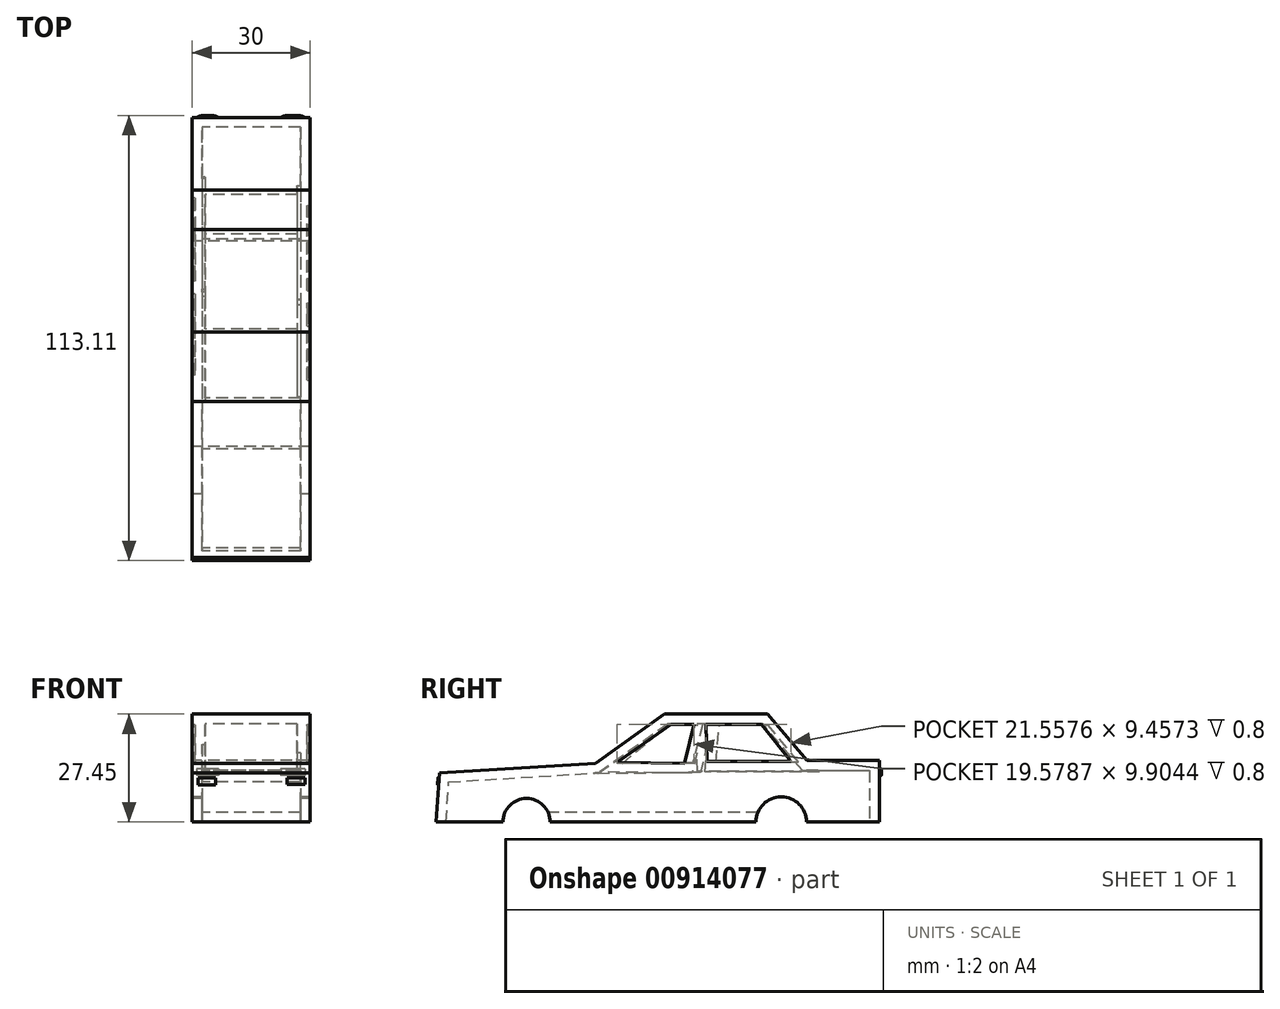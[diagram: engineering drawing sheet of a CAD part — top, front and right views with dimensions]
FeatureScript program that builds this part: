
annotation { "Feature Type Name" : "Feature", "Feature Type Description" : "" }
export const myFeature = defineFeature(function(context is Context, id is Id, definition is map)
    precondition{}
    {
        {
            var Q0;
            Q0=qCreatedBy(makeId("Right.planeOp"),FACE);
            var sketch = newSketch(context, id + "F0", { "sketchPlane" : qUnion([Q0])});
            skLineSegment(sketch, "E0", {"start": v(-54.31, 0) * mm, "end": v(-14.72, 2.41) * mm});
            skLineSegment(sketch, "E1", {"start": v(-14.72, 2.41) * mm, "end": v(2.91, 14.89) * mm});
            skLineSegment(sketch, "E2", {"start": v(2.91, 14.89) * mm, "end": v(29.03, 14.89) * mm});
            skLineSegment(sketch, "E3", {"start": v(29.03, 14.89) * mm, "end": v(39, 3.08) * mm});
            skLineSegment(sketch, "E4", {"start": v(39, 3.08) * mm, "end": v(57.47, 3.08) * mm});
            skLineSegment(sketch, "E5", {"start": v(57.47, 3.08) * mm, "end": v(57.47, -12.56) * mm});
            skLineSegment(sketch, "E6", {"start": v(57.47, -12.56) * mm, "end": v(-55.14, -12.56) * mm});
            skLineSegment(sketch, "E7", {"start": v(-55.14, -12.56) * mm, "end": v(-54.31, 0) * mm});
            skCircle(sketch, "E8", {"center": v(-32.19, -12.56) * mm, "radius": 6 * mm});
            skCircle(sketch, "E9", {"center": v(32.52, -12.56) * mm, "radius": 6.42 * mm});
            skSolve(sketch);
        }
        {
            var Q0;
            Q0=makeQuery(id+"F0.imprint","IMPRINT",FACE,{"disambiguationData":[TD([[makeQuery(id+"F0.imprint","IMPRINT",EDGE,{"derivedFrom":sQuery(id+"F0.wireOp",EDGE,"E0")}),-1.0]])]});
            extrude(context, id + "F1", {"entities" : qUnion([Q0]), "endBound" : BoundingType.SYMMETRIC, "depth" : 30 * mm, "offsetDistance" : 25 * mm});
        }
        {
            var Q0;
            Q0=makeQuery(id+"F1.opExtrude","CAP_FACE",FACE,{"disambiguationData":[OSD([sQuery(id+"F0.wireOp",EDGE,"E0"),sQuery(id+"F0.wireOp",EDGE,"E1"),sQuery(id+"F0.wireOp",EDGE,"E2"),sQuery(id+"F0.wireOp",EDGE,"E3"),sQuery(id+"F0.wireOp",EDGE,"E4"),sQuery(id+"F0.wireOp",EDGE,"E5"),sQuery(id+"F0.wireOp",EDGE,"E6"),sQuery(id+"F0.wireOp",EDGE,"E7"),sQuery(id+"F0.wireOp",EDGE,"E8"),sQuery(id+"F0.wireOp",EDGE,"E9")])],"isStart":false});
            var sketch = newSketch(context, id + "F2", { "sketchPlane" : qUnion([Q0])});
            skLineSegment(sketch, "E10", {"start": v(-9.25, 2.63) * mm, "end": v(4.45, 12.32) * mm});
            skLineSegment(sketch, "E11", {"start": v(4.45, 12.32) * mm, "end": v(10.33, 12.32) * mm});
            skLineSegment(sketch, "E12", {"start": v(10.33, 12.32) * mm, "end": v(7.91, 2.41) * mm});
            skLineSegment(sketch, "E13", {"start": v(7.91, 2.41) * mm, "end": v(-9.25, 2.63) * mm});
            skLineSegment(sketch, "E14", {"start": v(13.45, 12.32) * mm, "end": v(27.52, 12.32) * mm});
            skLineSegment(sketch, "E15", {"start": v(27.52, 12.32) * mm, "end": v(35, 2.86) * mm});
            skLineSegment(sketch, "E16", {"start": v(35, 2.86) * mm, "end": v(13.68, 2.86) * mm});
            skLineSegment(sketch, "E17", {"start": v(13.68, 2.86) * mm, "end": v(13.45, 12.32) * mm});
            skLineSegment(sketch, "E18.bottom", {"start": v(23.6, 12.32) * mm, "end": v(25.34, 12.32) * mm});
            skLineSegment(sketch, "E18.top", {"start": v(23.6, 2.86) * mm, "end": v(25.34, 2.86) * mm});
            skLineSegment(sketch, "E18.left", {"start": v(23.6, 12.32) * mm, "end": v(23.6, 2.86) * mm});
            skLineSegment(sketch, "E18.right", {"start": v(25.34, 12.32) * mm, "end": v(25.34, 2.86) * mm});
            skSolve(sketch);
        }
        {
            var Q0;
            Q0=makeQuery(id+"F2.imprint","IMPRINT",FACE,{"disambiguationData":[TD([[makeQuery(id+"F2.imprint","IMPRINT",EDGE,{"derivedFrom":sQuery(id+"F2.wireOp",EDGE,"E10")}),-1.0]])]});
            var Q1;
            Q1=makeQuery(id+"F2.imprint","IMPRINT",FACE,{"disambiguationData":[TD([[makeQuery(id+"F2.imprint","IMPRINT",EDGE,{"derivedFrom":sQuery(id+"F2.wireOp",EDGE,"E14")}),-1.0]])]});
            extrude(context, id + "F3", {"entities" : qUnion([Q0, Q1]), "operationType" : NewBodyOperationType.REMOVE, "oppositeDirection" : true, "depth" : 0.8 * mm, "offsetDistance" : 25 * mm});
        }
        {
            var Q0;
            Q0=makeQuery(id+"F1.opExtrude","CAP_FACE",FACE,{"disambiguationData":[OSD([sQuery(id+"F0.wireOp",EDGE,"E0"),sQuery(id+"F0.wireOp",EDGE,"E1"),sQuery(id+"F0.wireOp",EDGE,"E2"),sQuery(id+"F0.wireOp",EDGE,"E3"),sQuery(id+"F0.wireOp",EDGE,"E4"),sQuery(id+"F0.wireOp",EDGE,"E5"),sQuery(id+"F0.wireOp",EDGE,"E6"),sQuery(id+"F0.wireOp",EDGE,"E7"),sQuery(id+"F0.wireOp",EDGE,"E8"),sQuery(id+"F0.wireOp",EDGE,"E9")])],"isStart":true});
            var sketch = newSketch(context, id + "F4", { "sketchPlane" : qUnion([Q0])});
            skLineSegment(sketch, "E19", {"start": v(7.98, 2.3) * mm, "end": v(-3.78, 12.1) * mm});
            skLineSegment(sketch, "E20", {"start": v(-3.78, 12.1) * mm, "end": v(-12.55, 12.1) * mm});
            skLineSegment(sketch, "E21", {"start": v(-12.55, 12.1) * mm, "end": v(-10.01, 2.52) * mm});
            skLineSegment(sketch, "E22", {"start": v(-10.01, 2.52) * mm, "end": v(7.98, 2.3) * mm});
            skLineSegment(sketch, "E23", {"start": v(-16.81, 12.1) * mm, "end": v(-29.03, 12.1) * mm});
            skLineSegment(sketch, "E24", {"start": v(-29.03, 12.1) * mm, "end": v(-36.9, 2.64) * mm});
            skLineSegment(sketch, "E25", {"start": v(-36.9, 2.64) * mm, "end": v(-15.9, 2.64) * mm});
            skLineSegment(sketch, "E26", {"start": v(-15.9, 2.64) * mm, "end": v(-16.81, 12.1) * mm});
            skLineSegment(sketch, "E27.bottom", {"start": v(-26.48, 12.1) * mm, "end": v(-24.63, 12.1) * mm});
            skLineSegment(sketch, "E27.top", {"start": v(-26.48, 2.64) * mm, "end": v(-24.63, 2.64) * mm});
            skLineSegment(sketch, "E27.left", {"start": v(-26.48, 12.1) * mm, "end": v(-26.48, 2.64) * mm});
            skLineSegment(sketch, "E27.right", {"start": v(-24.63, 12.1) * mm, "end": v(-24.63, 2.64) * mm});
            skSolve(sketch);
        }
        {
            var Q0;
            Q0=makeQuery(id+"F4.imprint","IMPRINT",FACE,{"disambiguationData":[TD([[makeQuery(id+"F4.imprint","IMPRINT",EDGE,{"derivedFrom":sQuery(id+"F4.wireOp",EDGE,"E23")}),1.0]])]});
            var Q1;
            Q1=makeQuery(id+"F4.imprint","IMPRINT",FACE,{"disambiguationData":[TD([[makeQuery(id+"F4.imprint","IMPRINT",EDGE,{"derivedFrom":sQuery(id+"F4.wireOp",EDGE,"E19")}),1.0]])]});
            extrude(context, id + "F5", {"entities" : qUnion([Q0, Q1]), "operationType" : NewBodyOperationType.REMOVE, "oppositeDirection" : true, "depth" : 0.8 * mm, "offsetDistance" : 25 * mm});
        }
        {
            var Q0;
            Q0=makeQuery(id+"F1.opExtrude","SWEPT_FACE",FACE,{"disambiguationData":[OSD([sQuery(id+"F0.wireOp",EDGE,"E7")])]});
            var sketch = newSketch(context, id + "F6", { "sketchPlane" : qUnion([Q0])});
            skLineSegment(sketch, "E28.bottom", {"start": v(-13.44, -4.9) * mm, "end": v(-9.06, -4.9) * mm});
            skLineSegment(sketch, "E28.top", {"start": v(-13.44, -6.69) * mm, "end": v(-9.06, -6.69) * mm});
            skLineSegment(sketch, "E28.left", {"start": v(-13.44, -4.9) * mm, "end": v(-13.44, -6.69) * mm});
            skLineSegment(sketch, "E28.right", {"start": v(-9.06, -4.9) * mm, "end": v(-9.06, -6.69) * mm});
            skLineSegment(sketch, "E29.bottom", {"start": v(9.16, -4.95) * mm, "end": v(13.66, -4.95) * mm});
            skLineSegment(sketch, "E29.top", {"start": v(9.16, -6.6) * mm, "end": v(13.66, -6.6) * mm});
            skLineSegment(sketch, "E29.left", {"start": v(9.16, -4.95) * mm, "end": v(9.16, -6.6) * mm});
            skLineSegment(sketch, "E29.right", {"start": v(13.66, -4.95) * mm, "end": v(13.66, -6.6) * mm});
            skSolve(sketch);
        }
        {
            var Q0;
            Q0=makeQuery(id+"F6.imprint","IMPRINT",FACE,{"disambiguationData":[TD([[makeQuery(id+"F6.imprint","IMPRINT",EDGE,{"derivedFrom":sQuery(id+"F6.wireOp",EDGE,"E28.bottom")}),-1.0]])]});
            var Q1;
            Q1=makeQuery(id+"F6.imprint","IMPRINT",FACE,{"disambiguationData":[TD([[makeQuery(id+"F6.imprint","IMPRINT",EDGE,{"derivedFrom":sQuery(id+"F6.wireOp",EDGE,"E29.bottom")}),-1.0]])]});
            extrude(context, id + "F7", {"entities" : qUnion([Q0, Q1]), "operationType" : NewBodyOperationType.ADD, "depth" : 0.3 * mm, "offsetDistance" : 25 * mm});
        }
        {
            var Q0;
            Q0=makeQuery(id+"F7.opExtrude","CAP_EDGE",EDGE,{"disambiguationData":[OSD([sQuery(id+"F6.wireOp",EDGE,"E28.left")])],"isStart":false});
            var Q1;
            Q1=makeQuery(id+"F7.opExtrude","CAP_EDGE",EDGE,{"disambiguationData":[OSD([sQuery(id+"F6.wireOp",EDGE,"E28.right")])],"isStart":false});
            fillet(context, id + "F8", {"entities" : qUnion([Q0, Q1]), "radius" : 5 * mm, "tangentPropagation" : true, "allowEdgeOverflow" : false});
        }
        {
            var Q0;
            Q0=makeQuery(id+"F7.opExtrude","CAP_EDGE",EDGE,{"disambiguationData":[OSD([sQuery(id+"F6.wireOp",EDGE,"E29.left")])],"isStart":false});
            var Q1;
            Q1=makeQuery(id+"F7.opExtrude","CAP_EDGE",EDGE,{"disambiguationData":[OSD([sQuery(id+"F6.wireOp",EDGE,"E29.right")])],"isStart":false});
            fillet(context, id + "F9", {"entities" : qUnion([Q0, Q1]), "radius" : 5 * mm, "tangentPropagation" : true, "allowEdgeOverflow" : false});
        }
        {
            var Q0;
            {var subQ0=sQuery(id+"F0.wireOp",EDGE,"E6");Q0=makeQuery(id+"F1.opExtrude","SWEPT_FACE",FACE,{"disambiguationData":[OSD([subQ0]),TDD([makeQuery(id+"F0.imprint","IMPRINT",EDGE,{"disambiguationData":[TD([[makeQuery(id+"F0.imprint","INTERSECT",VERTEX,{"disambiguationData":[OD(1.0)],"derivedFrom":[subQ0,sQuery(id+"F0.wireOp",EDGE,"E9")]}),-1.0]])],"derivedFrom":subQ0})])]});}
            var Q1;
            {var subQ0=sQuery(id+"F0.wireOp",EDGE,"E6");Q1=makeQuery(id+"F1.opExtrude","SWEPT_FACE",FACE,{"disambiguationData":[OSD([subQ0]),TDD([makeQuery(id+"F0.imprint","IMPRINT",EDGE,{"disambiguationData":[TD([[makeQuery(id+"F0.imprint","INTERSECT",VERTEX,{"derivedFrom":[subQ0,sQuery(id+"F0.wireOp",EDGE,"E7")]}),1.0]])],"derivedFrom":subQ0})])]});}
            var Q2;
            {var subQ0=sQuery(id+"F0.wireOp",EDGE,"E6");Q2=makeQuery(id+"F1.opExtrude","SWEPT_FACE",FACE,{"disambiguationData":[OSD([subQ0]),TDD([makeQuery(id+"F0.imprint","IMPRINT",EDGE,{"disambiguationData":[TD([[makeQuery(id+"F0.imprint","INTERSECT",VERTEX,{"derivedFrom":[sQuery(id+"F0.wireOp",EDGE,"E5"),subQ0]}),-1.0]])],"derivedFrom":subQ0})])]});}
            var Q3;
            Q3=makeQuery(id+"F1.opExtrude","SWEPT_FACE",FACE,{"disambiguationData":[OSD([sQuery(id+"F0.wireOp",EDGE,"E8")])]});
            var Q4;
            Q4=makeQuery(id+"F1.opExtrude","SWEPT_FACE",FACE,{"disambiguationData":[OSD([sQuery(id+"F0.wireOp",EDGE,"E9")])]});
            shell(context, id + "F10", {"entities" : qUnion([Q0, Q1, Q2, Q3, Q4]), "thickness" : 2.5 * mm});
        }
        {
            var Q0;
            Q0=makeQuery(id+"F1.opExtrude","SWEPT_FACE",FACE,{"disambiguationData":[OSD([sQuery(id+"F0.wireOp",EDGE,"E5")])]});
            var sketch = newSketch(context, id + "F11", { "sketchPlane" : qUnion([Q0])});
            skLineSegment(sketch, "E30.bottom", {"start": v(-13.7, 0.93) * mm, "end": v(-7.45, 0.93) * mm});
            skLineSegment(sketch, "E30.top", {"start": v(-13.7, -0.65) * mm, "end": v(-7.45, -0.65) * mm});
            skLineSegment(sketch, "E30.left", {"start": v(-13.7, 0.93) * mm, "end": v(-13.7, -0.65) * mm});
            skLineSegment(sketch, "E30.right", {"start": v(-7.45, 0.93) * mm, "end": v(-7.45, -0.65) * mm});
            skLineSegment(sketch, "E31.bottom", {"start": v(8.25, 0.93) * mm, "end": v(13.88, 0.93) * mm});
            skLineSegment(sketch, "E31.top", {"start": v(8.25, -0.72) * mm, "end": v(13.88, -0.72) * mm});
            skLineSegment(sketch, "E31.left", {"start": v(8.25, 0.93) * mm, "end": v(8.25, -0.72) * mm});
            skLineSegment(sketch, "E31.right", {"start": v(13.88, 0.93) * mm, "end": v(13.88, -0.72) * mm});
            skSolve(sketch);
        }
        {
            var Q0;
            Q0=makeQuery(id+"F11.imprint","IMPRINT",FACE,{"disambiguationData":[TD([[makeQuery(id+"F11.imprint","IMPRINT",EDGE,{"derivedFrom":sQuery(id+"F11.wireOp",EDGE,"E30.bottom")}),-1.0]])]});
            var Q1;
            Q1=makeQuery(id+"F11.imprint","IMPRINT",FACE,{"disambiguationData":[TD([[makeQuery(id+"F11.imprint","IMPRINT",EDGE,{"derivedFrom":sQuery(id+"F11.wireOp",EDGE,"E31.bottom")}),-1.0]])]});
            extrude(context, id + "F12", {"entities" : qUnion([Q0, Q1]), "operationType" : NewBodyOperationType.ADD, "depth" : 0.5 * mm, "offsetDistance" : 25 * mm});
        }
        {
            var Q0;
            Q0=makeQuery(id+"F12.opExtrude","CAP_EDGE",EDGE,{"disambiguationData":[OSD([sQuery(id+"F11.wireOp",EDGE,"E30.right")])],"isStart":false});
            var Q1;
            Q1=makeQuery(id+"F12.opExtrude","CAP_EDGE",EDGE,{"disambiguationData":[OSD([sQuery(id+"F11.wireOp",EDGE,"E30.left")])],"isStart":false});
            var Q2;
            Q2=makeQuery(id+"F12.opExtrude","CAP_EDGE",EDGE,{"disambiguationData":[OSD([sQuery(id+"F11.wireOp",EDGE,"E31.left")])],"isStart":false});
            var Q3;
            Q3=makeQuery(id+"F12.opExtrude","CAP_EDGE",EDGE,{"disambiguationData":[OSD([sQuery(id+"F11.wireOp",EDGE,"E31.right")])],"isStart":false});
            fillet(context, id + "F13", {"entities" : qUnion([Q0, Q1, Q2, Q3]), "radius" : 5 * mm, "tangentPropagation" : true, "allowEdgeOverflow" : false});
        }
    });
